# Revit family: Gira_107900
name_source: partatom
category: Electrical Fixtures
revit_build: Autodesk Revit 2017 (Build: 20160225_1515(x64)
units: mm (PartAtom-declared; Revit-internal decimal feet)

## family parameters
Cut with Voids When Loaded = No
Host = Face
Maintain Annotation Orientation = No
Part Type = Normal
Room Calculation Point = No
Round Connector Dimension = Use Diameter
Shared = No

## types (1)
- Pow.supply 640 mA w/o choke KNX DRA
    BIM = https://media.live.bim.site 16f.rfa
    BIMSITE_PRODUCT_ID = dcdc9d8b2239130fc9737134f1ddaba9afbbed0b
    Bus connection included = No
    Cost = 0 $
    Default Elevation = 1219 mm
    Description = PS 640 mA w o choke DRA KNX KNX power supply 640 mA uninterruptible,DRA Features: - The uninterruptible power supply 640 mA generates the KNX system voltage. - With integrated choke for de-coupling the bus line from the power supply. - With connections for a lead-gel rechargeable accumulators for buffering KNX voltage in case of a mains failure. - Up to two lead-gel rechargeable accumulators can be connected and charged via the uninterruptible power supply. - The charging voltage is controlled depending on the temperature using a temperature sensor. - The uninterruptible power supply has a zero-voltage 2-way switch for reporting a fault (e.g. mains failure, battery failure, overload, or short circuit).,Notes : - Connection is made via KNX bus connection or junction terminals (no data rail required). - Recommendation: Overvoltage protection for Gira KNX products. - Overvoltage diverter BUStector BT 24, manufacturer: DEHN + SÖHNE, Article No. 925001.
    GTIN = 4010337009115
    HAN = 107900
    HeinzeBIM = https://www.heinze.de
    Local operation/hand operation = No
    Manufacturer = Gira
    Number of integrated choke coils = 0
    Rated current [Ampere] = 0
    Suitable for C-load = No
    URL = https://www.gira.de

## geometry (parser evidence)
native form markers: Blend x2, Sweep x3
no freeform markers — native parametric forms only
